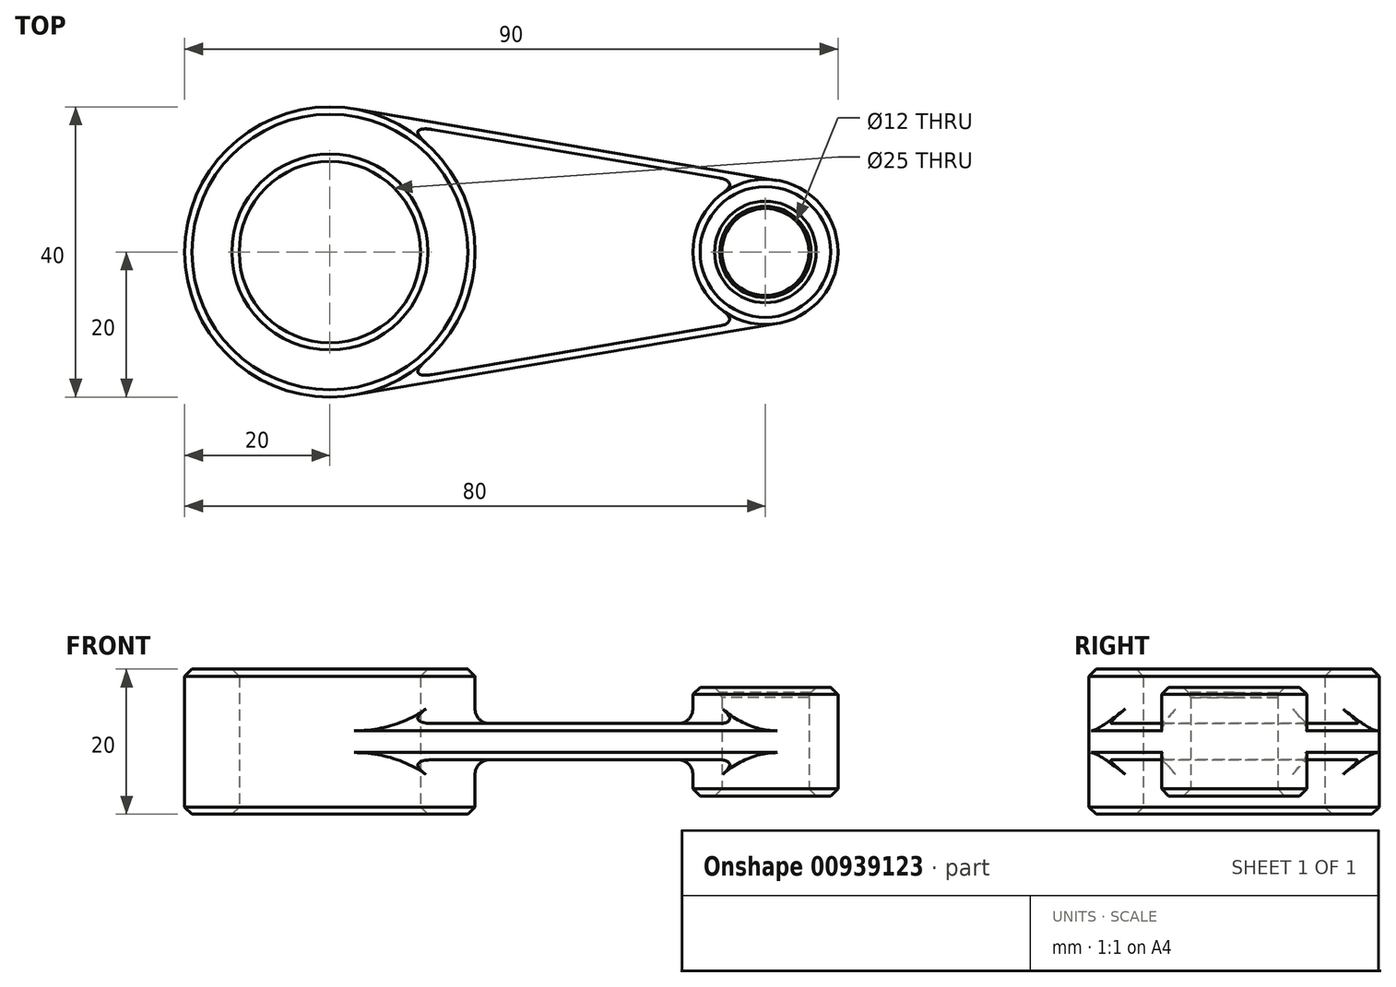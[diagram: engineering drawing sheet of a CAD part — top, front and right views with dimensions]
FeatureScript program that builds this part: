
annotation { "Feature Type Name" : "Feature", "Feature Type Description" : "" }
export const myFeature = defineFeature(function(context is Context, id is Id, definition is map)
    precondition{}
    {
        {
            var Q0;
            Q0=qCreatedBy(makeId("Top.planeOp"),FACE);
            var sketch = newSketch(context, id + "F0", { "sketchPlane" : qUnion([Q0])});
            skCircle(sketch, "E0", {"center": v(0, 0) * mm, "radius": 20 * mm});
            skCircle(sketch, "E1", {"center": v(60, 0) * mm, "radius": 10 * mm});
            skLineSegment(sketch, "E2", {"start": v(3.33, -19.72) * mm, "end": v(61.67, -9.86) * mm});
            skLineSegment(sketch, "E3", {"start": v(3.33, 19.72) * mm, "end": v(61.67, 9.86) * mm});
            skCircle(sketch, "E4", {"center": v(0, 0) * mm, "radius": 12.5 * mm});
            skCircle(sketch, "E5", {"center": v(60, 0) * mm, "radius": 6 * mm});
            skSolve(sketch);
        }
        {
            var Q0;
            Q0=makeQuery(id+"F0.imprint","IMPRINT",FACE,{"disambiguationData":[TD([[makeQuery(id+"F0.imprint","IMPRINT",EDGE,{"derivedFrom":sQuery(id+"F0.wireOp",EDGE,"E4")}),-1.0]])]});
            var Q1;
            {var subQ0=sQuery(id+"F0.wireOp",EDGE,"E2");Q1=makeQuery(id+"F0.imprint","IMPRINT",FACE,{"disambiguationData":[TD([[makeQuery(id+"F0.imprint","IMPRINT",EDGE,{"derivedFrom":subQ0}),1.0]])]});}
            var Q2;
            Q2=makeQuery(id+"F0.imprint","IMPRINT",FACE,{"disambiguationData":[TD([[makeQuery(id+"F0.imprint","IMPRINT",EDGE,{"derivedFrom":sQuery(id+"F0.wireOp",EDGE,"E5")}),-1.0]])]});
            extrude(context, id + "F1", {"entities" : qUnion([Q0, Q1, Q2]), "endBound" : BoundingType.SYMMETRIC, "depth" : 5 * mm, "offsetDistance" : 25 * mm});
        }
        {
            var Q0;
            Q0=makeQuery(id+"F0.imprint","IMPRINT",FACE,{"disambiguationData":[TD([[makeQuery(id+"F0.imprint","IMPRINT",EDGE,{"derivedFrom":sQuery(id+"F0.wireOp",EDGE,"E5")}),-1.0]])]});
            extrude(context, id + "F2", {"entities" : qUnion([Q0]), "operationType" : NewBodyOperationType.ADD, "endBound" : BoundingType.SYMMETRIC, "depth" : 15 * mm, "offsetDistance" : 25 * mm});
        }
        {
            var Q0;
            Q0=makeQuery(id+"F0.imprint","IMPRINT",FACE,{"disambiguationData":[TD([[makeQuery(id+"F0.imprint","IMPRINT",EDGE,{"derivedFrom":sQuery(id+"F0.wireOp",EDGE,"E4")}),-1.0]])]});
            extrude(context, id + "F3", {"entities" : qUnion([Q0]), "operationType" : NewBodyOperationType.ADD, "endBound" : BoundingType.SYMMETRIC, "depth" : 20 * mm, "offsetDistance" : 25 * mm});
        }
        {
            var Q0;
            Q0=makeQuery(id+"F3.opExtrude","CAP_EDGE",EDGE,{"disambiguationData":[OSD([sQuery(id+"F0.wireOp",EDGE,"E4")])],"isStart":false});
            var Q1;
            Q1=makeQuery(id+"F2.opExtrude","CAP_EDGE",EDGE,{"disambiguationData":[OSD([sQuery(id+"F0.wireOp",EDGE,"E5")])],"isStart":false});
            chamfer(context, id + "F4", {"entities" : qUnion([Q0, Q1]), "width" : 1 * mm, "tangentPropagation" : true});
        }
        {
            var Q0;
            Q0=makeQuery(id+"F3.opExtrude","CAP_EDGE",EDGE,{"disambiguationData":[OSD([sQuery(id+"F0.wireOp",EDGE,"E4")])],"isStart":true});
            var Q1;
            {var subQ0=sQuery(id+"F0.wireOp",EDGE,"E5");Q1=makeQuery(id+"F2.boolean.opBoolean","MERGE",FACE,{"derivedFrom":[makeQuery(id+"F1.opExtrude","SWEPT_FACE",FACE,{"disambiguationData":[OSD([subQ0])]}),makeQuery(id+"F2.opExtrude","SWEPT_FACE",FACE,{"disambiguationData":[OSD([subQ0])]})]});}
            chamfer(context, id + "F5", {"entities" : qUnion([Q0, Q1]), "width" : 1 * mm, "tangentPropagation" : true});
        }
        {
            var Q0;
            Q0=makeQuery(id+"F3.opExtrude","CAP_EDGE",EDGE,{"disambiguationData":[OSD([sQuery(id+"F0.wireOp",EDGE,"E0")])],"isStart":true});
            var Q1;
            Q1=makeQuery(id+"F2.opExtrude","CAP_EDGE",EDGE,{"disambiguationData":[OSD([sQuery(id+"F0.wireOp",EDGE,"E1")])],"isStart":true});
            chamfer(context, id + "F6", {"entities" : qUnion([Q0, Q1]), "width" : 1 * mm, "tangentPropagation" : true});
        }
        {
            var Q0;
            Q0=makeQuery(id+"F3.opExtrude","CAP_EDGE",EDGE,{"disambiguationData":[OSD([sQuery(id+"F0.wireOp",EDGE,"E0")])],"isStart":false});
            var Q1;
            Q1=makeQuery(id+"F2.opExtrude","CAP_EDGE",EDGE,{"disambiguationData":[OSD([sQuery(id+"F0.wireOp",EDGE,"E1")])],"isStart":false});
            chamfer(context, id + "F7", {"entities" : qUnion([Q0, Q1]), "width" : 1 * mm, "tangentPropagation" : true});
        }
        {
            var Q0;
            Q0=makeQuery(id+"F1.opExtrude","CAP_EDGE",EDGE,{"disambiguationData":[OSD([sQuery(id+"F0.wireOp",EDGE,"E3")])],"isStart":false});
            var Q1;
            Q1=makeQuery(id+"F1.opExtrude","CAP_EDGE",EDGE,{"disambiguationData":[OSD([sQuery(id+"F0.wireOp",EDGE,"E2")])],"isStart":false});
            var Q2;
            Q2=makeQuery(id+"F1.opExtrude","CAP_EDGE",EDGE,{"disambiguationData":[OSD([sQuery(id+"F0.wireOp",EDGE,"E2")])],"isStart":true});
            var Q3;
            Q3=makeQuery(id+"F1.opExtrude","CAP_EDGE",EDGE,{"disambiguationData":[OSD([sQuery(id+"F0.wireOp",EDGE,"E3")])],"isStart":true});
            chamfer(context, id + "F8", {"entities" : qUnion([Q0, Q1, Q2, Q3]), "width" : 1 * mm, "tangentPropagation" : true});
        }
        {
            var Q0;
            {var subQ0=sQuery(id+"F0.wireOp",EDGE,"E0");Q0=makeQuery(id+"F3.boolean.opBoolean","INTERSECT",EDGE,{"derivedFrom":[makeQuery(id+"F1.opExtrude","CAP_FACE",FACE,{"disambiguationData":[OSD([subQ0,sQuery(id+"F0.wireOp",EDGE,"E1"),sQuery(id+"F0.wireOp",EDGE,"E2"),sQuery(id+"F0.wireOp",EDGE,"E3"),sQuery(id+"F0.wireOp",EDGE,"E4"),sQuery(id+"F0.wireOp",EDGE,"E5")])],"isStart":false}),makeQuery(id+"F3.opExtrude","SWEPT_FACE",FACE,{"disambiguationData":[OSD([subQ0])]})]});}
            var Q1;
            {var subQ0=sQuery(id+"F0.wireOp",EDGE,"E1");Q1=makeQuery(id+"F2.boolean.opBoolean","INTERSECT",EDGE,{"derivedFrom":[makeQuery(id+"F1.opExtrude","CAP_FACE",FACE,{"disambiguationData":[OSD([sQuery(id+"F0.wireOp",EDGE,"E0"),subQ0,sQuery(id+"F0.wireOp",EDGE,"E2"),sQuery(id+"F0.wireOp",EDGE,"E3"),sQuery(id+"F0.wireOp",EDGE,"E4"),sQuery(id+"F0.wireOp",EDGE,"E5")])],"isStart":false}),makeQuery(id+"F2.opExtrude","SWEPT_FACE",FACE,{"disambiguationData":[OSD([subQ0])]})]});}
            var Q2;
            {var subQ0=sQuery(id+"F0.wireOp",EDGE,"E0");Q2=makeQuery(id+"F3.boolean.opBoolean","INTERSECT",EDGE,{"derivedFrom":[makeQuery(id+"F1.opExtrude","CAP_FACE",FACE,{"disambiguationData":[OSD([subQ0,sQuery(id+"F0.wireOp",EDGE,"E1"),sQuery(id+"F0.wireOp",EDGE,"E2"),sQuery(id+"F0.wireOp",EDGE,"E3"),sQuery(id+"F0.wireOp",EDGE,"E4"),sQuery(id+"F0.wireOp",EDGE,"E5")])],"isStart":true}),makeQuery(id+"F3.opExtrude","SWEPT_FACE",FACE,{"disambiguationData":[OSD([subQ0])]})]});}
            var Q3;
            {var subQ0=sQuery(id+"F0.wireOp",EDGE,"E1");Q3=makeQuery(id+"F2.boolean.opBoolean","INTERSECT",EDGE,{"derivedFrom":[makeQuery(id+"F1.opExtrude","CAP_FACE",FACE,{"disambiguationData":[OSD([sQuery(id+"F0.wireOp",EDGE,"E0"),subQ0,sQuery(id+"F0.wireOp",EDGE,"E2"),sQuery(id+"F0.wireOp",EDGE,"E3"),sQuery(id+"F0.wireOp",EDGE,"E4"),sQuery(id+"F0.wireOp",EDGE,"E5")])],"isStart":true}),makeQuery(id+"F2.opExtrude","SWEPT_FACE",FACE,{"disambiguationData":[OSD([subQ0])]})]});}
            fillet(context, id + "F9", {"entities" : qUnion([Q0, Q1, Q2, Q3]), "radius" : 2 * mm, "tangentPropagation" : true, "allowEdgeOverflow" : false});
        }
    });
